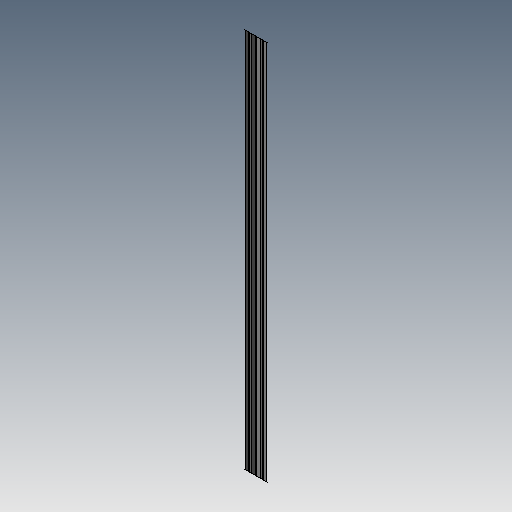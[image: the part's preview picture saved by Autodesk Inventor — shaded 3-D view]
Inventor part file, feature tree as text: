
AUTODESK INVENTOR PART (.ipt)
format: ipt  version: 2020 (Build 240168000, 168)  size: 259,072 bytes
history: native  units: mm (DEFAULTED — no unit token found)
features: other x21, sketch x5, extrude x3, hole x2, pattern_linear x1
ambient origin geometry x8: Origin, YZ Plane, XZ Plane, XY Plane, X Axis, Y Axis, Z Axis, Center Point
bodies: Solid1 (feature_tree)
feature tree (32):
  extrude  "Extrusion1"  Depth=2.0mm
  hole  "Hole1"  [1 undecoded]
  hole  "Hole2"  [1 undecoded]
  pattern_linear  "Rectangular Pattern1"  [2 undecoded]
  extrude  "Extrusion2"  [1 undecoded]
  extrude  "Extrusion3"  [1 undecoded]
  other  "C1_XY"
  other  "C1_YZ"
  other  "C1_ZX"
  other  "C1_X"
  other  "C1_Y"
  other  "C1_Z"
  other  "C1_Center"
  other  "to_frame_cap1_XY"
  other  "to_frame_cap1_YZ"
  other  "to_frame_cap1_ZX"
  other  "to_frame_cap1_X"
  other  "to_frame_cap1_Y"
  other  "to_frame_cap1_Z"
  other  "to_frame_cap1_Center"
  other  "to_frame_cap2_XY"
  other  "to_frame_cap2_YZ"
  other  "to_frame_cap2_ZX"
  other  "to_frame_cap2_X"
  other  "to_frame_cap2_Y"
  other  "to_frame_cap2_Z"
  other  "to_frame_cap2_Center"
  sketch  "Sketch_1"  dims[d0=1005.5mm d1=0.0mm]
  sketch  "Sketch2"  dims[d2=6.8mm d3=6.0mm d4=4.0mm d5=2.0mm d6=90.0deg d7=1005.5mm d8=0.0mm]
  sketch  "Sketch3"  dims[d9=4.2mm d10=6.0mm d11=4.0mm d12=2.0mm d13=90.0deg d14=1005.5mm d15=0.0mm d16=20.0mm d18=23.2mm d19=20.0mm d21=23.2mm]
  sketch  "Sketch_5"  dims[d22=30.0mm d23=0.0mm d24=30.0mm d25=0.0mm]
  sketch  "Sketch_8"
note: 6 required parameter values undecoded (feature->parameter linkage not recoverable at this tier; creation-order binding heuristic only, values carry confidence <= 0.55)
